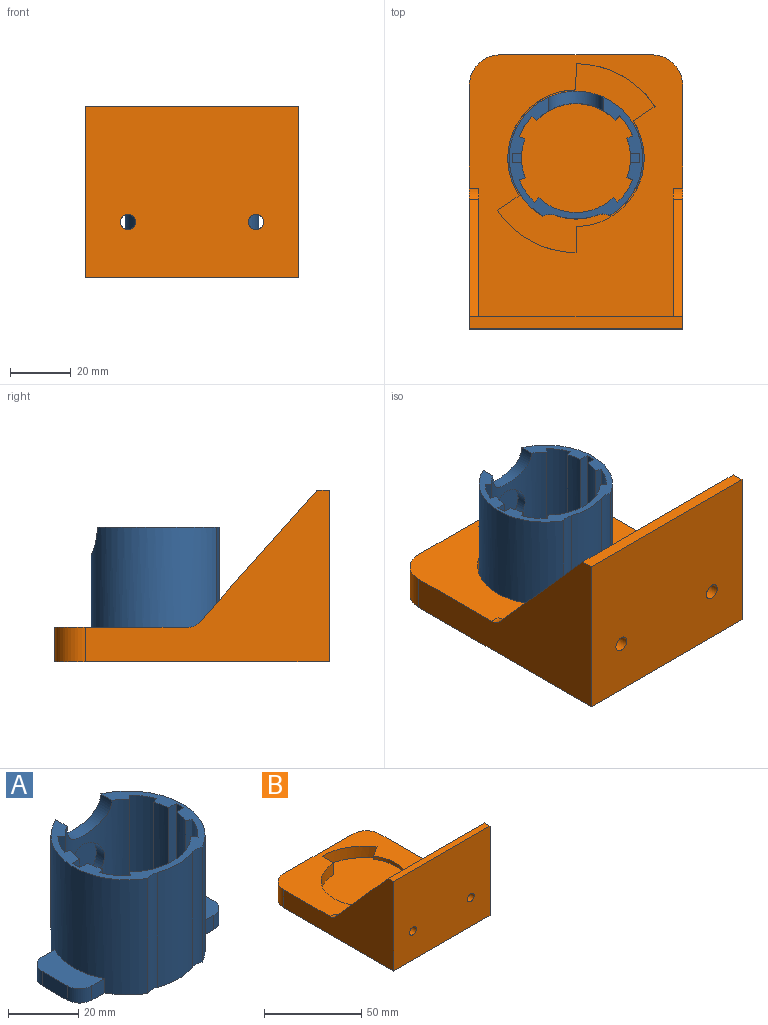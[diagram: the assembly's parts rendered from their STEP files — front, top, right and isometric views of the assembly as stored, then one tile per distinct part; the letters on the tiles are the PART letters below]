
ASSEMBLY  parts=2 mates=1
PART A: 45 faces, bbox 59x41.9x40 mm
  f0: cylinder r=21.9mm len=43.8mm, axis (0,0,-1), area 4248.9mm2, adj f5,f6,f15,f31,f32,f33,f34,f38
  f1: cylinder r=17.9mm len=40mm, axis (0,0,-1), area 407.3mm2, adj f5,f6,f7,f9,f10,f19,f29
  f2: cylinder r=17.9mm len=40mm, axis (0,0,-1), area 867.1mm2, adj f5,f6,f15,f16,f26,f27
  f3: cylinder r=17.9mm len=40mm, axis (0,0,-1), area 412.7mm2, adj f5,f6,f11,f12,f14,f21,f24
  f4: cylinder r=17.9mm len=40mm, axis (0,0,-1), area 1077.1mm2, adj f5,f6,f18,f22
  f5: plane 43.8x39.97mm, normal (0,0,1), area 305.5mm2, adj f0,f1,f2,f3,f4,f7,f8,f9
  f6: plane 58.97x41.9mm, normal (0,0,-1), area 711.3mm2, adj f0,f1,f2,f3,f4,f18,f19,f20
  f7: plane 38x3mm, normal (0,-1,0), area 114mm2, adj f1,f5,f8,f10
  f8: plane 38x3mm, normal (1,0,0), area 114mm2, adj f5,f7,f9,f10
  f9: plane 38x3mm, normal (0,1,0), area 114mm2, adj f1,f5,f8,f10
  f10: plane 3x3mm, normal (0,0,1), area 8.9mm2, adj f1,f7,f8,f9
  f11: plane 38x3mm, normal (0,-1,0), area 114mm2, adj f3,f5,f13,f14
  f12: plane 38x3mm, normal (0,1,0), area 114mm2, adj f3,f5,f13,f14
  f13: plane 38x3mm, normal (-1,0,0), area 114mm2, adj f5,f11,f12,f14
  f14: plane 3x3mm, normal (0,0,1), area 8.9mm2, adj f3,f11,f12,f13
  f15: cylinder r=9mm len=18mm, axis (0,-1,0), area 119.8mm2, adj f0,f2,f5
  f16: cylinder r=7mm len=14mm, axis (0,-1,0), area 110.2mm2, adj f2,f17
  f17: plane 14x14mm, normal (0,-1,0), area 153.9mm2, adj f16
  f18: plane 40x1.46mm, normal (-0.73,0.69,0), area 80mm2, adj f4,f5,f6,f20
  f19: plane 40x1.87mm, normal (0.36,-0.93,0), area 80mm2, adj f1,f5,f6,f20
  f20: cylinder r=19.9mm len=40mm, axis (0,0,1), area 358.8mm2, adj f5,f6,f18,f19
  f21: plane 40x1.86mm, normal (-0.36,-0.93,0), area 80mm2, adj f3,f5,f6,f23
  f22: plane 40x1.47mm, normal (0.73,0.68,0), area 80mm2, adj f4,f5,f6,f23
  f23: cylinder r=19.9mm len=40mm, axis (0,0,1), area 358.8mm2, adj f5,f6,f21,f22
  f24: plane 40x1.87mm, normal (-0.36,0.93,0), area 80mm2, adj f3,f5,f6,f25
  f25: cylinder r=19.9mm len=40mm, axis (0,0,1), area 318.1mm2, adj f5,f6,f24,f26
  f26: plane 40x1.44mm, normal (0.69,-0.72,0), area 80mm2, adj f2,f5,f6,f25
  f27: plane 40x1.44mm, normal (-0.69,-0.72,0), area 80mm2, adj f2,f5,f6,f28
  f28: cylinder r=19.9mm len=40mm, axis (0,0,1), area 318.1mm2, adj f5,f6,f27,f29
  f29: plane 40x1.87mm, normal (0.36,0.93,0), area 80mm2, adj f1,f5,f6,f28
  f30: cylinder r=20mm len=40mm, axis (0,0,1), area 569.2mm2, adj f5,f6,f31,f32
  f31: cylinder r=5mm len=40mm, axis (0,0,-1), area 164.2mm2, adj f0,f5,f6,f30
  f32: cylinder r=5mm len=40mm, axis (0,0,-1), area 164.2mm2, adj f0,f5,f6,f30
  f33: plane 5x5mm, normal (0,-1,0), area 25mm2, adj f0,f6,f37,f38
  f34: plane 5x5mm, normal (0,1,0), area 25mm2, adj f0,f6,f35,f38
  f35: cylinder r=5mm len=5mm, axis (0,0,-1), area 39.3mm2, adj f6,f34,f36,f38
  f36: plane 10x5mm, normal (-1,0,0), area 50mm2, adj f6,f35,f37,f38
  f37: cylinder r=5mm len=5mm, axis (0,0,-1), area 39.3mm2, adj f6,f33,f36,f38
  f38: plane 20x10mm, normal (0,0,1), area 156.7mm2, adj f0,f33,f34,f35,f36,f37
  f39: plane 5x5mm, normal (0,-1,0), area 25mm2, adj f0,f6,f40,f44
  f40: cylinder r=5mm len=5mm, axis (0,0,-1), area 39.3mm2, adj f6,f39,f41,f44
  f41: plane 10x5mm, normal (1,0,0), area 50mm2, adj f6,f40,f42,f44
  f42: cylinder r=5mm len=5mm, axis (0,0,-1), area 39.3mm2, adj f6,f41,f43,f44
  f43: plane 5x5mm, normal (0,1,0), area 25mm2, adj f0,f6,f42,f44
  f44: plane 20x10mm, normal (0,0,1), area 156.7mm2, adj f0,f39,f40,f41,f42,f43
PART B: 31 faces, bbox 70x90x56.3 mm
  f0: plane 64x45mm, normal (0,1,0), area 2840.7mm2, adj f2,f22,f23,f25,f27,f28
  f1: plane 70x56.3mm, normal (0,-1,0), area 3901.7mm2, adj f3,f5,f6,f22,f27,f28
  f2: plane 86x70mm, normal (0,0,1), area 3693.2mm2, adj f0,f3,f4,f5,f7,f9,f10,f11
  f3: plane 80x56.3mm, normal (1,0,0), area 1984.7mm2, adj f1,f2,f6,f20,f22,f24,f30
  f4: plane 50x11.3mm, normal (0,1,0), area 565mm2, adj f2,f6,f20,f21
  f5: plane 80x56.3mm, normal (-1,0,0), area 1984.7mm2, adj f1,f2,f6,f21,f22,f26,f29
  f6: plane 90x70mm, normal (0,0,-1), area 6257.1mm2, adj f1,f3,f4,f5,f20,f21
  f7: cylinder r=31mm len=41.55mm, axis (0,0,-1), area 376.7mm2, adj f2,f8,f14,f15,f16,f19
  f8: plane 9.39x5.3mm, normal (0,1,0), area 49.8mm2, adj f7,f9,f15,f19
  f9: cylinder r=22.4mm len=34.66mm, axis (0,0,-1), area 224.5mm2, adj f2,f8,f10,f15,f16,f19
  f10: plane 8.6x7.3mm, normal (-1,0,0), area 62.8mm2, adj f2,f9,f11,f19
  f11: cylinder r=31mm len=41.38mm, axis (0,0,-1), area 375.3mm2, adj f2,f10,f12,f17,f18,f19
  f12: plane 9.36x5.3mm, normal (0,-1,0), area 49.6mm2, adj f11,f13,f18,f19
  f13: cylinder r=22.4mm len=34.77mm, axis (0,0,-1), area 225.9mm2, adj f2,f12,f14,f17,f18,f19
  f14: plane 8.6x7.3mm, normal (1,0,0), area 62.8mm2, adj f2,f7,f13,f19
  f15: plane 27.52x12.25mm, normal (0,0,-1), area 226.4mm2, adj f7,f8,f9,f16
  f16: plane 7.2x4.71mm, normal (-0.55,0.84,0), area 17.2mm2, adj f2,f7,f9,f15
  f17: plane 7.17x4.75mm, normal (0.55,-0.83,0), area 17.2mm2, adj f2,f11,f13,f18
  f18: plane 27.5x12.33mm, normal (0,0,-1), area 226.1mm2, adj f11,f12,f13,f17
  f19: plane 62x62mm, normal (0,0,1), area 2482.8mm2, adj f7,f8,f9,f10,f11,f12,f13,f14
  f20: cylinder r=10mm len=11.3mm, axis (0,0,1), area 177.5mm2, adj f2,f3,f4,f6
  f21: cylinder r=10mm len=11.3mm, axis (0,0,-1), area 177.5mm2, adj f2,f4,f5,f6
  f22: plane 70x4mm, normal (0,0,1), area 280mm2, adj f0,f1,f3,f5,f24,f26
  f23: plane 45x42.25mm, normal (-1,0,0), area 900.7mm2, adj f0,f2,f24,f30
  f24: plane 43.32x38.51mm, normal (0,0.75,0.66), area 173.9mm2, adj f3,f22,f23,f30
  f25: plane 45x42.25mm, normal (1,0,0), area 900.7mm2, adj f0,f2,f26,f29
  f26: plane 43.32x38.51mm, normal (0,0.75,0.66), area 173.9mm2, adj f5,f22,f25,f29
  f27: cylinder r=2.5mm len=5mm, axis (0,-1,0), area 62.8mm2, adj f0,f1
  f28: cylinder r=2.5mm len=5mm, axis (0,-1,0), area 62.8mm2, adj f0,f1
  f29: cylinder r=5mm len=3.74mm, axis (1,0,0), area 12.7mm2, adj f2,f5,f25,f26
  f30: cylinder r=5mm len=3.74mm, axis (-1,0,0), area 12.7mm2, adj f2,f3,f23,f24
PLACE A rot(axis=(0,0,1),0.3deg) t=(-34.04,-1.67,12.46)mm
PLACE B t=(-34.04,-1.67,10.26)mm fixed
MATE cylindrical B.f9 <-> A.f1  axis (0,0,1) through (-34.04,-1.67,12.26)mm
